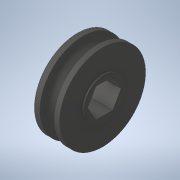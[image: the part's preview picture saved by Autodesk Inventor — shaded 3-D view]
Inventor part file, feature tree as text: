
AUTODESK INVENTOR PART (.ipt)
format: ipt  version: 2022.3 (Build 263350000, 350)  size: 169,472 bytes
history: native  units: in
note: dims shown in document units (in); Inventor stores cm internally (conversion verified against a paired STEP export)
features: fillet x1
ambient origin geometry x8: Origin, YZ Plane, XZ Plane, XY Plane, X Axis, Y Axis, Z Axis, Center Point
bodies: Solid1 (feature_tree)
feature tree (1):
  fillet  "Fillet1"  [1 undecoded]
note: 1 required parameter value undecoded (feature->parameter linkage not recoverable at this tier; creation-order binding heuristic only, values carry confidence <= 0.55)
